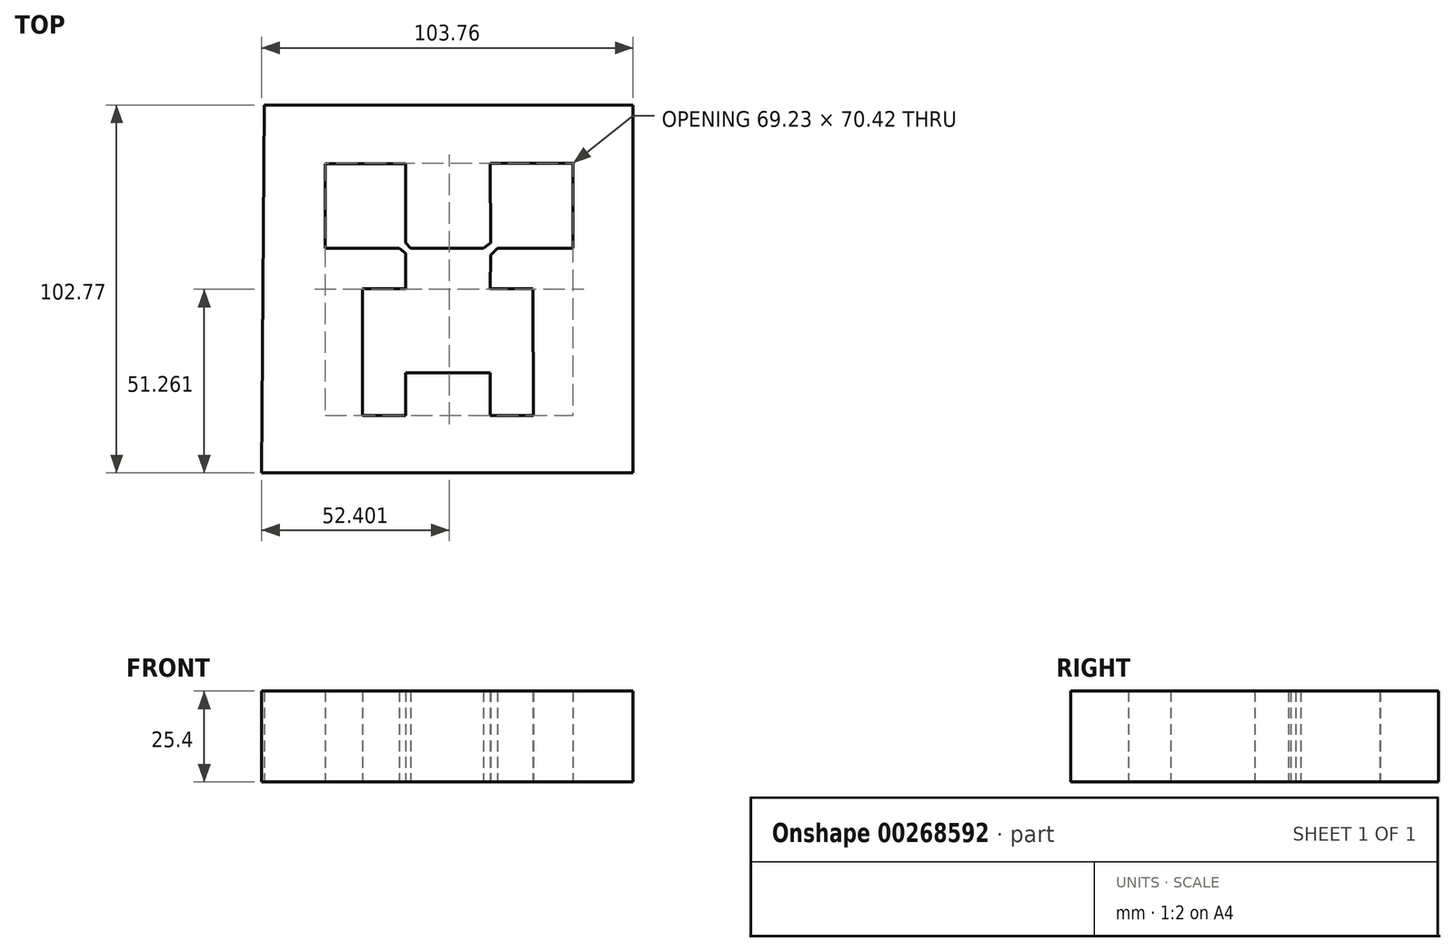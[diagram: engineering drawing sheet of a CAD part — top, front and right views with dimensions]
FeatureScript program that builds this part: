
annotation { "Feature Type Name" : "Feature", "Feature Type Description" : "" }
export const myFeature = defineFeature(function(context is Context, id is Id, definition is map)
    precondition{}
    {
        {
            var Q0;
            Q0=qCreatedBy(makeId("Top.planeOp"),FACE);
            var sketch = newSketch(context, id + "F0", { "sketchPlane" : qUnion([Q0])});
            skLineSegment(sketch, "E0", {"start": v(-65.68, 57.27) * mm, "end": v(-65.68, -64.05) * mm});
            skLineSegment(sketch, "E1", {"start": v(-65.68, -64.05) * mm, "end": v(55.64, -64.05) * mm});
            skLineSegment(sketch, "E2", {"start": v(55.64, 57.27) * mm, "end": v(55.64, -64.05) * mm});
            skLineSegment(sketch, "E3", {"start": v(-57.18, -55.27) * mm, "end": v(46.58, -55.27) * mm});
            skLineSegment(sketch, "E4", {"start": v(46.58, -55.27) * mm, "end": v(46.58, 47.5) * mm});
            skLineSegment(sketch, "E5", {"start": v(46.58, 47.5) * mm, "end": v(-56.47, 47.5) * mm});
            skLineSegment(sketch, "E6", {"start": v(-56.47, 47.5) * mm, "end": v(-57.18, -55.27) * mm});
            skLineSegment(sketch, "E7", {"start": v(6.74, 31.2) * mm, "end": v(29.84, 31.2) * mm});
            skLineSegment(sketch, "E8", {"start": v(29.84, 31.2) * mm, "end": v(29.84, 7.51) * mm});
            skLineSegment(sketch, "E9", {"start": v(29.84, 7.51) * mm, "end": v(8.68, 7.51) * mm});
            skLineSegment(sketch, "E10", {"start": v(6.75, 8.96) * mm, "end": v(6.74, 31.2) * mm});
            skLineSegment(sketch, "E11", {"start": v(18.63, -3.89) * mm, "end": v(6.74, -3.89) * mm});
            skPoint(sketch, "E11.startSnap0", {"position": v(46.58, -3.89) * mm});
            skLineSegment(sketch, "E12", {"start": v(6.74, -3.89) * mm, "end": v(6.74, 5.57) * mm});
            skLineSegment(sketch, "E13", {"start": v(-16.88, 6.12) * mm, "end": v(-16.88, -3.89) * mm});
            skLineSegment(sketch, "E14", {"start": v(-16.88, -3.89) * mm, "end": v(-28.95, -3.89) * mm});
            skLineSegment(sketch, "E15", {"start": v(-28.95, -3.89) * mm, "end": v(-28.95, -39.22) * mm});
            skLineSegment(sketch, "E16", {"start": v(-28.95, -39.22) * mm, "end": v(-16.88, -39.22) * mm});
            skLineSegment(sketch, "E17", {"start": v(-16.88, -39.22) * mm, "end": v(-16.88, -27.37) * mm});
            skLineSegment(sketch, "E18", {"start": v(-16.88, -27.37) * mm, "end": v(6.74, -27.37) * mm});
            skLineSegment(sketch, "E19", {"start": v(6.74, -27.37) * mm, "end": v(6.74, -39.22) * mm});
            skLineSegment(sketch, "E20", {"start": v(6.74, -39.22) * mm, "end": v(18.7, -39.22) * mm});
            skLineSegment(sketch, "E21", {"start": v(18.7, -39.22) * mm, "end": v(18.63, -3.89) * mm});
            skLineSegment(sketch, "E22", {"start": v(-15.52, 7.51) * mm, "end": v(4.73, 7.51) * mm});
            skLineSegment(sketch, "E23", {"start": v(-16.88, 31.04) * mm, "end": v(-39.4, 31.04) * mm});
            skLineSegment(sketch, "E24", {"start": v(-39.4, 31.04) * mm, "end": v(-39.4, 7.51) * mm});
            skLineSegment(sketch, "E25", {"start": v(-39.4, 7.51) * mm, "end": v(-18.68, 7.51) * mm});
            skLineSegment(sketch, "E26", {"start": v(-16.88, 31.04) * mm, "end": v(-16.88, 8.94) * mm});
            skLineSegment(sketch, "E27", {"start": v(-18.68, 7.51) * mm, "end": v(-16.88, 6.12) * mm});
            skLineSegment(sketch, "E28", {"start": v(-16.88, 8.94) * mm, "end": v(-15.52, 7.51) * mm});
            skPoint(sketch, "E29.orphan", {"position": v(-16.88, 7.51) * mm});
            skLineSegment(sketch, "E30", {"start": v(6.75, 8.96) * mm, "end": v(4.73, 7.51) * mm});
            skLineSegment(sketch, "E31", {"start": v(6.74, 5.57) * mm, "end": v(8.68, 7.51) * mm});
            skPoint(sketch, "E32.orphan", {"position": v(6.75, 7.51) * mm});
            skSolve(sketch);
        }
        {
            var Q0;
            Q0 = qSketchRegion(id + "F0", true);
            extrude(context, id + "F1", {"entities" : qUnion([Q0]), "depth" : 25.4 * mm});
        }
    });
